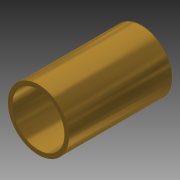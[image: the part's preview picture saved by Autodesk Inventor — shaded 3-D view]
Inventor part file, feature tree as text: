
AUTODESK INVENTOR PART (.ipt)
format: ipt  version: 2014 SP1 (Build 180222100, 222)  size: 88,064 bytes
history: native  units: in
note: dims shown in document units (in); Inventor stores cm internally (conversion verified against a paired STEP export)
features: extrude x1, sketch x1
ambient origin geometry x8: Origin, YZ Plane, XZ Plane, XY Plane, X Axis, Y Axis, Z Axis, Center Point
bodies: Solid1 (feature_tree)
feature tree (2):
  extrude  "Extrusion1"  Depth=0.7438in
  sketch  "Sketch1"  dims[d0=0.379in d2=0.437in d3=0.7438in d4=0.0in]
